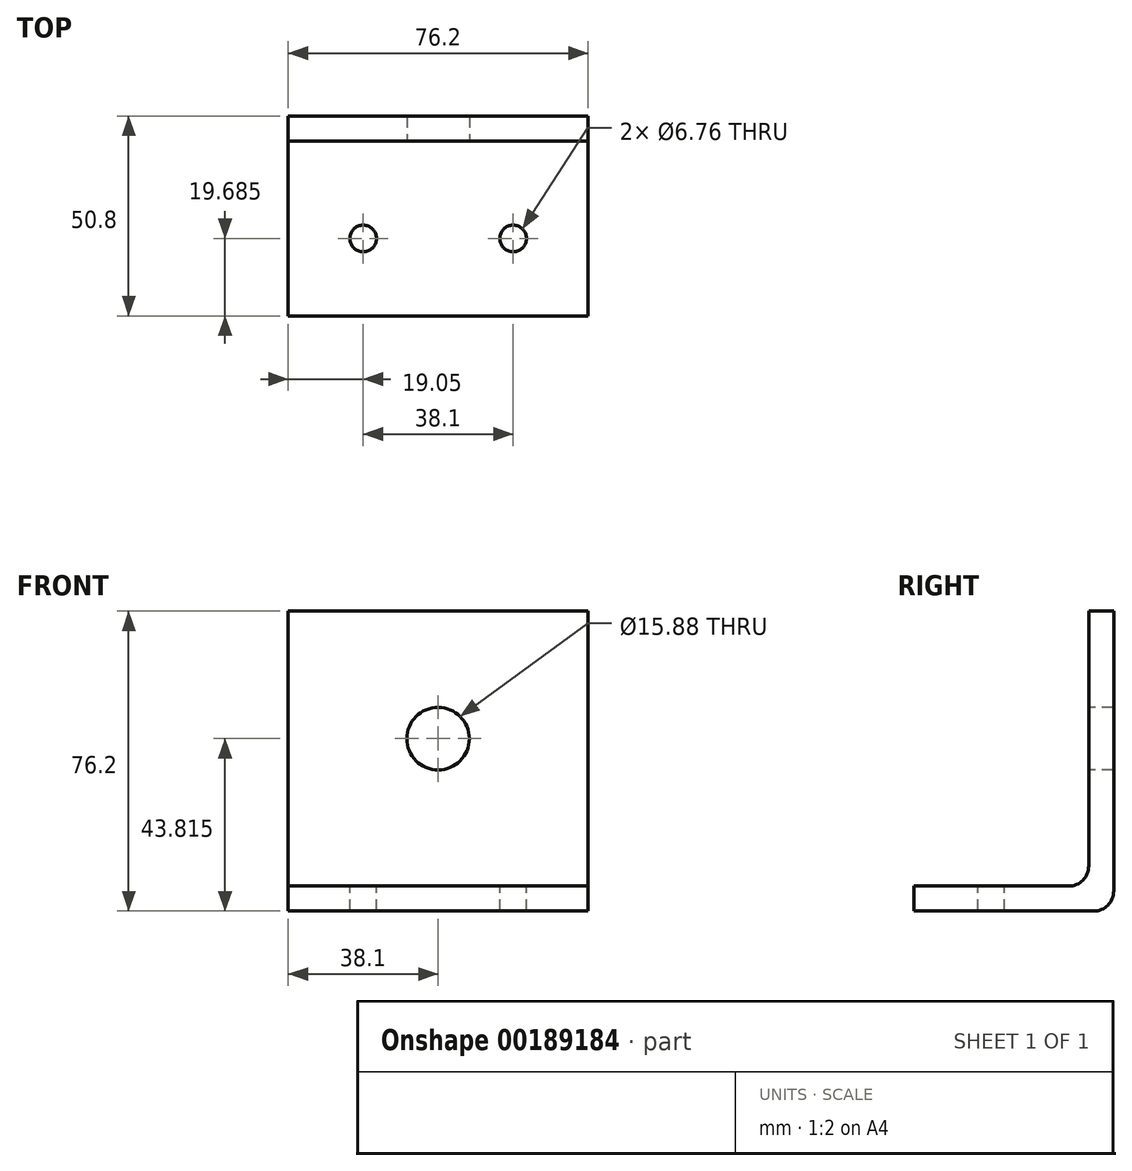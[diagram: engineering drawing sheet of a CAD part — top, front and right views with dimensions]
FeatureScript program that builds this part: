
annotation { "Feature Type Name" : "Feature", "Feature Type Description" : "" }
export const myFeature = defineFeature(function(context is Context, id is Id, definition is map)
    precondition{}
    {
        {
            var Q0;
            Q0=qCreatedBy(makeId("Right.planeOp"),FACE);
            var sketch = newSketch(context, id + "F0", { "sketchPlane" : qUnion([Q0])});
            skLineSegment(sketch, "E0.bottom", {"start": v(0, 0) * mm, "end": v(50.8, 0) * mm});
            skLineSegment(sketch, "E0.right", {"start": v(50.8, 0) * mm, "end": v(50.8, 76.2) * mm});
            skLineSegment(sketch, "E1.bottom", {"start": v(3.18, 6.35) * mm, "end": v(44.45, 6.35) * mm});
            skLineSegment(sketch, "E1.right", {"start": v(44.45, 6.35) * mm, "end": v(44.45, 50.8) * mm});
            skPoint(sketch, "E1.top.start.orphan", {"position": v(3.17, 47.63) * mm});
            skPoint(sketch, "E0.top.start.orphan", {"position": v(0, 50.8) * mm});
            skLineSegment(sketch, "E2", {"start": v(50.8, 76.2) * mm, "end": v(44.45, 76.2) * mm});
            skLineSegment(sketch, "E3", {"start": v(44.45, 76.2) * mm, "end": v(44.45, 50.8) * mm});
            skLineSegment(sketch, "E4", {"start": v(0, 0) * mm, "end": v(0, 6.35) * mm});
            skLineSegment(sketch, "E5", {"start": v(0, 6.35) * mm, "end": v(3.18, 6.35) * mm});
            skSolve(sketch);
        }
        {
            var Q0;
            Q0 = qSketchRegion(id + "F0", true);
            extrude(context, id + "F1", {"entities" : qUnion([Q0]), "endBound" : BoundingType.SYMMETRIC, "depth" : 76.2 * mm});
        }
        {
            var Q0;
            Q0=makeQuery(id+"F1.opExtrude","SWEPT_EDGE",EDGE,{"disambiguationData":[OSD([sQuery(id+"F0.wireOp",EDGE,"E0.bottom"),sQuery(id+"F0.wireOp",EDGE,"E0.right")])]});
            var Q1;
            Q1=makeQuery(id+"F1.opExtrude","SWEPT_EDGE",EDGE,{"disambiguationData":[OSD([sQuery(id+"F0.wireOp",EDGE,"E1.bottom"),sQuery(id+"F0.wireOp",EDGE,"E1.right")])]});
            fillet(context, id + "F2", {"entities" : qUnion([Q0, Q1]), "radius" : 5.08 * mm, "tangentPropagation" : true, "allowEdgeOverflow" : false});
        }
        {
            var Q0;
            Q0=makeQuery(id+"F1.opExtrude","SWEPT_FACE",FACE,{"disambiguationData":[OSD([sQuery(id+"F0.wireOp",EDGE,"E1.bottom"),sQuery(id+"F0.wireOp",EDGE,"E5")])]});
            var sketch = newSketch(context, id + "F3", { "sketchPlane" : qUnion([Q0])});
            skCircle(sketch, "E6", {"center": v(19.05, 19.68) * mm, "radius": 3.38 * mm});
            skPoint(sketch, "E6.centerSnap0", {"position": v(38.1, 19.68) * mm});
            skCircle(sketch, "E7", {"center": v(-19.05, 19.69) * mm, "radius": 3.38 * mm});
            skPoint(sketch, "E7.centerSnap0", {"position": v(-38.1, 19.68) * mm});
            skSolve(sketch);
        }
        {
            var Q0;
            Q0 = qSketchRegion(id + "F3", true);
            var Q1;
            Q1 = qConstructionFilter(qBodyType(qCreatedBy(id + "F3" ,EDGE), BodyType.WIRE), ConstructionObject.NO);
            extrude(context, id + "F4", {"entities" : qUnion([Q0]), "operationType" : NewBodyOperationType.REMOVE, "surfaceEntities" : qUnion([Q1]), "endBound" : BoundingType.THROUGH_ALL, "oppositeDirection" : true, "depth" : 25.4 * mm});
        }
        {
            var Q0;
            Q0=makeQuery(id+"F1.opExtrude","SWEPT_FACE",FACE,{"disambiguationData":[OSD([sQuery(id+"F0.wireOp",EDGE,"E1.right"),sQuery(id+"F0.wireOp",EDGE,"E3")])]});
            var sketch = newSketch(context, id + "F5", { "sketchPlane" : qUnion([Q0])});
            skCircle(sketch, "E8", {"center": v(0, 43.81) * mm, "radius": 7.94 * mm});
            skPoint(sketch, "E8.centerSnap0", {"position": v(-38.1, 43.81) * mm});
            skSolve(sketch);
        }
        {
            var Q0;
            Q0 = qSketchRegion(id + "F5", true);
            extrude(context, id + "F6", {"entities" : qUnion([Q0]), "operationType" : NewBodyOperationType.REMOVE, "endBound" : BoundingType.THROUGH_ALL, "oppositeDirection" : true, "depth" : 25.4 * mm});
        }
    });
